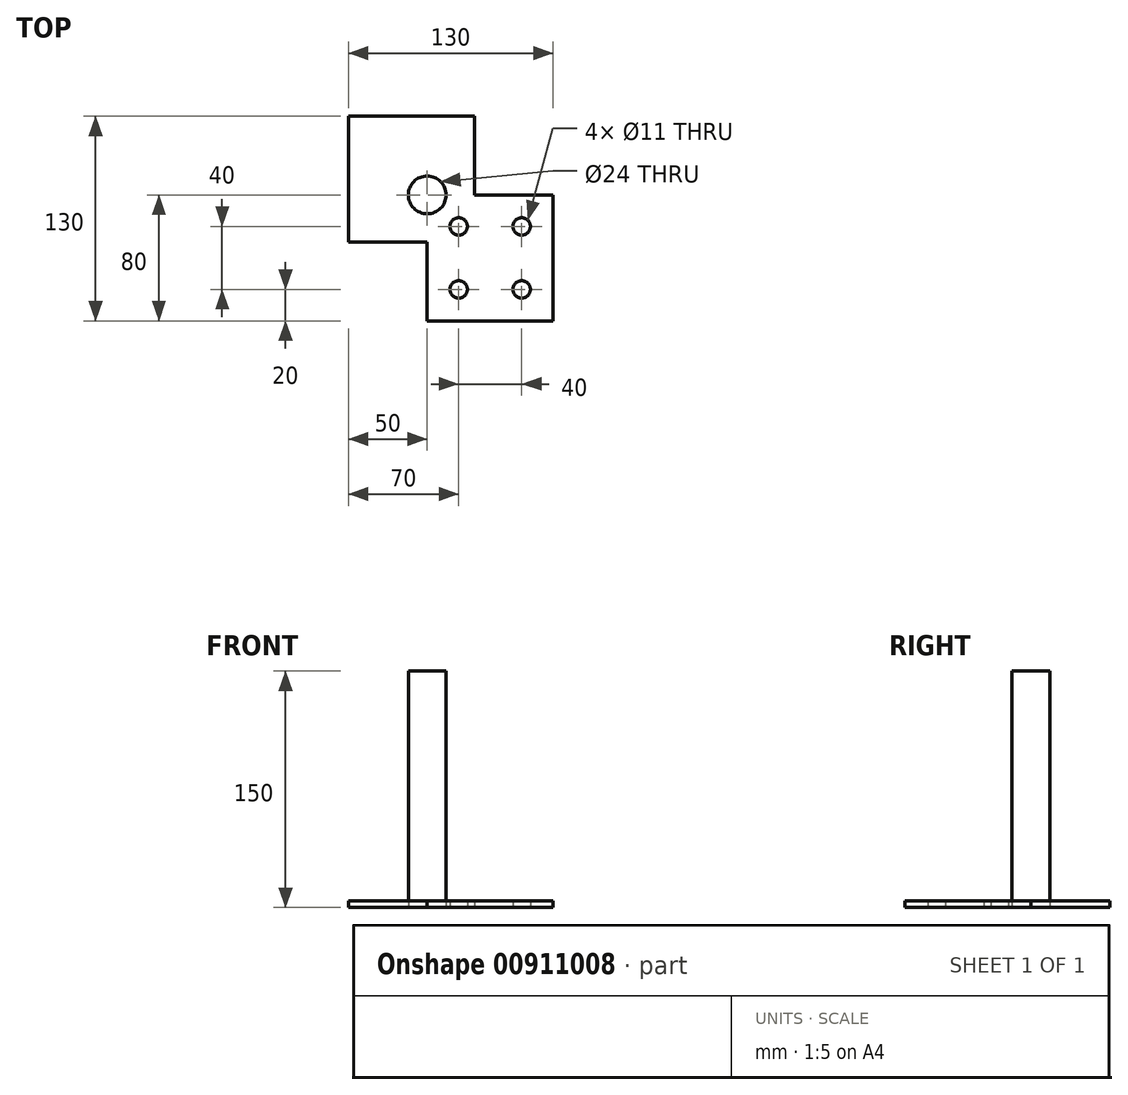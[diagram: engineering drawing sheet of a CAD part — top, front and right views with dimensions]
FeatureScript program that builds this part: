
annotation { "Feature Type Name" : "Feature", "Feature Type Description" : "" }
export const myFeature = defineFeature(function(context is Context, id is Id, definition is map)
    precondition{}
    {
        {
            var Q0;
            Q0=qCreatedBy(makeId("Top.planeOp"),FACE);
            var sketch = newSketch(context, id + "F0", { "sketchPlane" : qUnion([Q0])});
            skCircle(sketch, "E0", {"center": v(0, 0) * mm, "radius": 12 * mm});
            skLineSegment(sketch, "E1.left", {"start": v(-50, 50) * mm, "end": v(-50, -30) * mm});
            skLineSegment(sketch, "E2", {"start": v(-50, 50) * mm, "end": v(30, 50) * mm});
            skLineSegment(sketch, "E3", {"start": v(30, 50) * mm, "end": v(30, 0) * mm});
            skLineSegment(sketch, "E4", {"start": v(30, 0) * mm, "end": v(80, 0) * mm});
            skLineSegment(sketch, "E5", {"start": v(-50, -30) * mm, "end": v(0, -30) * mm});
            skLineSegment(sketch, "E6", {"start": v(0, -30) * mm, "end": v(0, -80) * mm});
            skLineSegment(sketch, "E7", {"start": v(0, -80) * mm, "end": v(80, -80) * mm});
            skLineSegment(sketch, "E8", {"start": v(80, -80) * mm, "end": v(80, 0) * mm});
            skCircle(sketch, "E9", {"center": v(60, -20) * mm, "radius": 5.5 * mm});
            skCircle(sketch, "E10", {"center": v(60, -60) * mm, "radius": 5.5 * mm});
            skLineSegment(sketch, "E11", {"start": v(40, -80) * mm, "end": v(40, 0) * mm, "construction": true});
            skCircle(sketch, "E12.MirrorC", {"center": v(20, -20) * mm, "radius": 5.5 * mm});
            skCircle(sketch, "E13.MirrorC", {"center": v(20, -60) * mm, "radius": 5.5 * mm});
            skSolve(sketch);
        }
        {
            var Q0;
            Q0=makeQuery(id+"F0.imprint","IMPRINT",FACE,{"disambiguationData":[TD([[makeQuery(id+"F0.imprint","IMPRINT",EDGE,{"derivedFrom":sQuery(id+"F0.wireOp",EDGE,"E0")}),-1.0]])]});
            extrude(context, id + "F1", {"entities" : qUnion([Q0]), "depth" : 4 * mm, "offsetDistance" : 25 * mm});
        }
        {
            var Q0;
            Q0=makeQuery(id+"F1.opExtrude","CAP_FACE",FACE,{"disambiguationData":[OSD([sQuery(id+"F0.wireOp",EDGE,"E0"),sQuery(id+"F0.wireOp",EDGE,"E1.left"),sQuery(id+"F0.wireOp",EDGE,"E2"),sQuery(id+"F0.wireOp",EDGE,"E3"),sQuery(id+"F0.wireOp",EDGE,"E4"),sQuery(id+"F0.wireOp",EDGE,"E5"),sQuery(id+"F0.wireOp",EDGE,"E6"),sQuery(id+"F0.wireOp",EDGE,"E7"),sQuery(id+"F0.wireOp",EDGE,"E8"),sQuery(id+"F0.wireOp",EDGE,"E9"),sQuery(id+"F0.wireOp",EDGE,"E10"),sQuery(id+"F0.wireOp",EDGE,"E12.MirrorC"),sQuery(id+"F0.wireOp",EDGE,"E13.MirrorC")])],"isStart":true});
            var sketch = newSketch(context, id + "F2", { "sketchPlane" : qUnion([Q0])});
            skCircle(sketch, "E14", {"center": v(0, 0) * mm, "radius": 12 * mm});
            skSolve(sketch);
        }
        {
            var Q0;
            Q0=makeQuery(id+"F2.imprint","IMPRINT",FACE,{"disambiguationData":[TD([[makeQuery(id+"F2.imprint","IMPRINT",EDGE,{"derivedFrom":sQuery(id+"F2.wireOp",EDGE,"E14")}),-1.0]])]});
            extrude(context, id + "F3", {"entities" : qUnion([Q0]), "oppositeDirection" : true, "depth" : 150 * mm, "offsetDistance" : 25 * mm});
        }
    });
